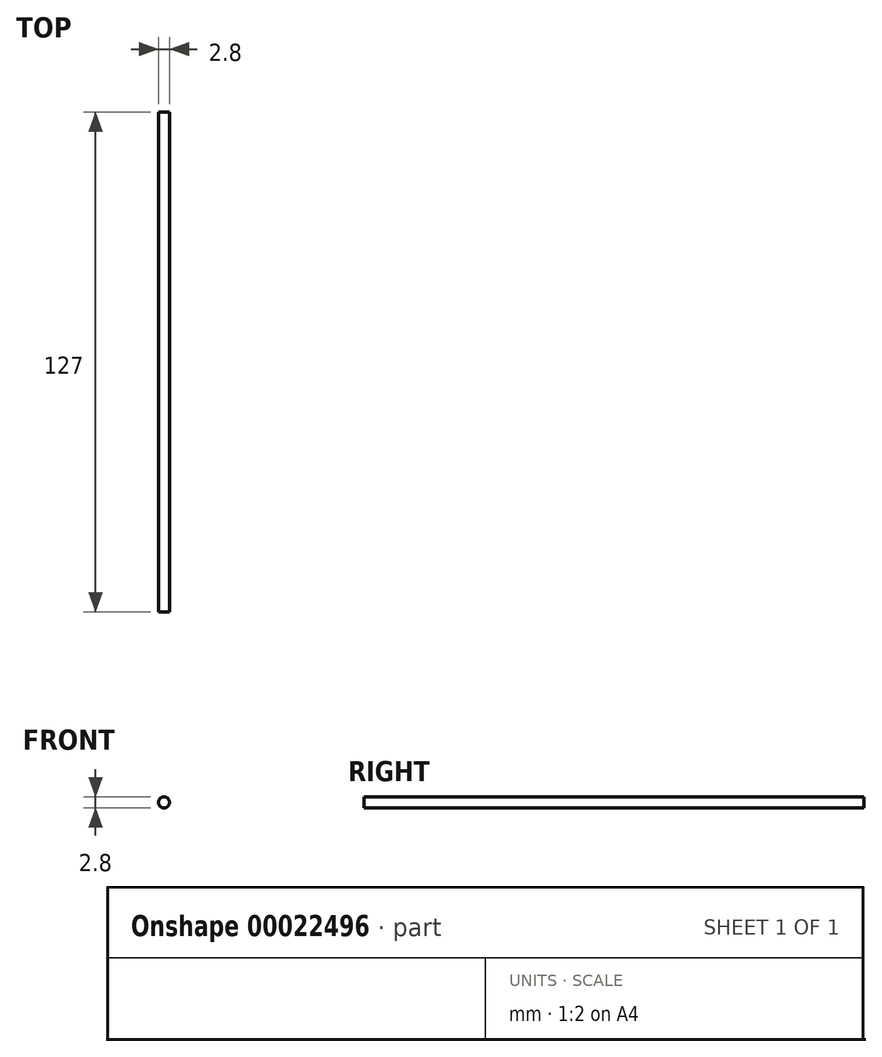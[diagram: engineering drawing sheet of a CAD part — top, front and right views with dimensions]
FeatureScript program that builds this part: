
annotation { "Feature Type Name" : "Feature", "Feature Type Description" : "" }
export const myFeature = defineFeature(function(context is Context, id is Id, definition is map)
    precondition{}
    {
        {
            var Q0;
            Q0=qCreatedBy(makeId("Front.planeOp"),FACE);
            var sketch = newSketch(context, id + "F0", { "sketchPlane" : qUnion([Q0])});
            skCircle(sketch, "E0", {"center": v(-17.01, 31.82) * mm, "radius": 1.4 * mm});
            skSolve(sketch);
        }
        {
            var Q0;
            Q0 = qSketchRegion(id + "F0", true);
            var Q1;
            Q1=makeQuery(id+"F0.imprint","IMPRINT",FACE,{"disambiguationData":[TD([[makeQuery(id+"F0.imprint","IMPRINT",EDGE,{"derivedFrom":sQuery(id+"F0.wireOp",EDGE,"E0")}),1.0]])]});
            extrude(context, id + "F1", {"entities" : qUnion([Q0, Q1]), "depth" : 127 * mm});
        }
    });
